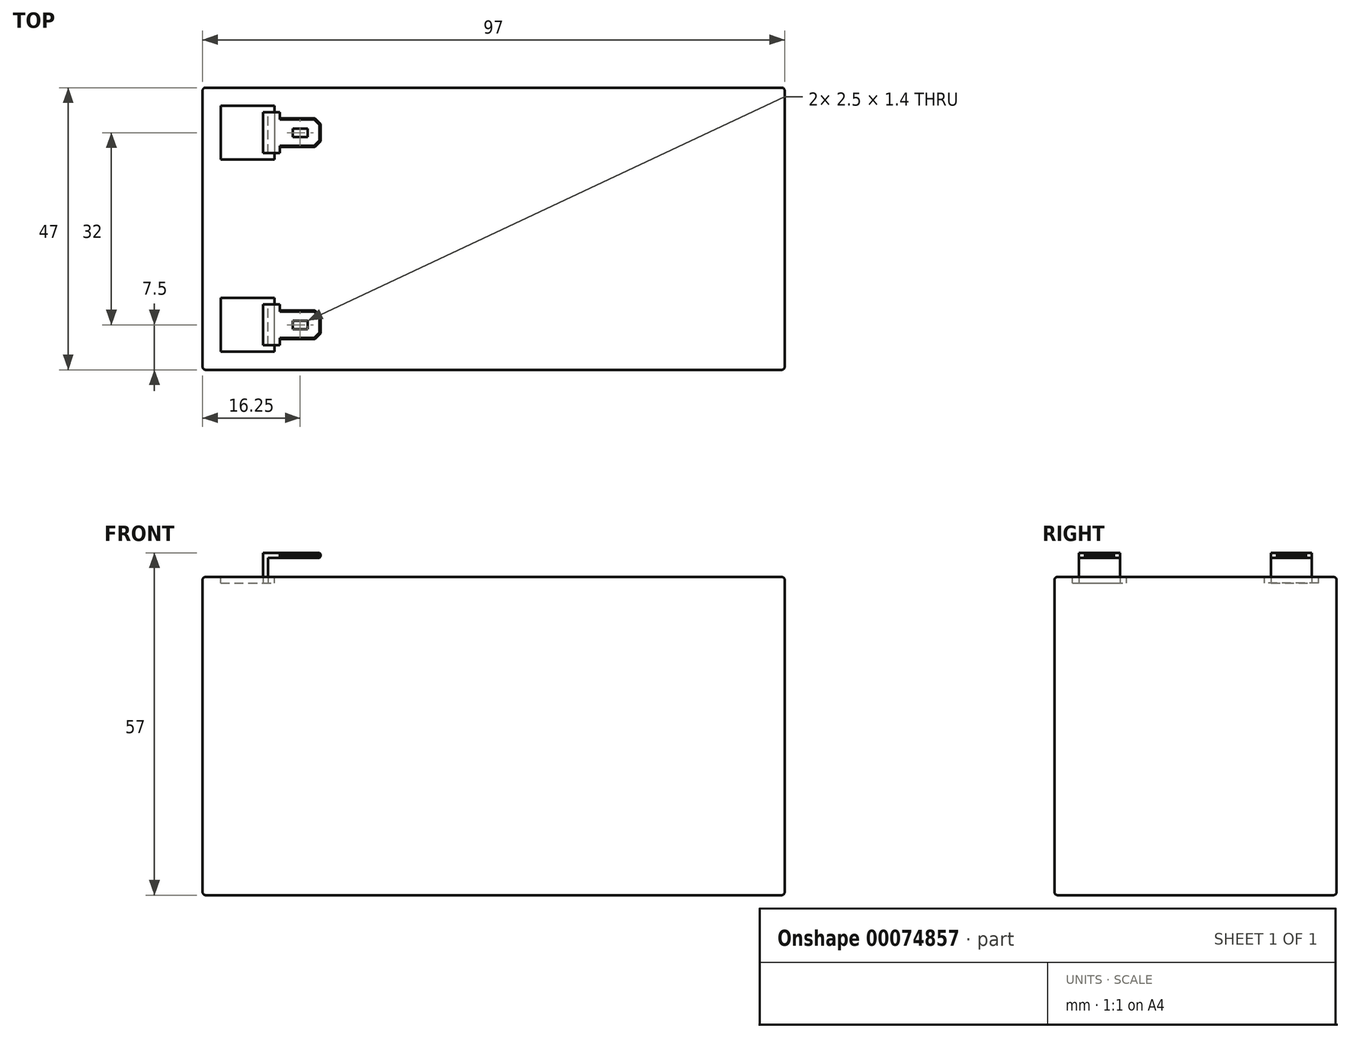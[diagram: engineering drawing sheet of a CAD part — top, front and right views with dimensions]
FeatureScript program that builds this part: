
annotation { "Feature Type Name" : "Feature", "Feature Type Description" : "" }
export const myFeature = defineFeature(function(context is Context, id is Id, definition is map)
    precondition{}
    {
        {
            var Q0;
            Q0=qCreatedBy(makeId("Top.planeOp"),FACE);
            var sketch = newSketch(context, id + "F0", { "sketchPlane" : qUnion([Q0])});
            skLineSegment(sketch, "E0.bottom", {"start": v(0, 0) * mm, "end": v(97, 0) * mm});
            skLineSegment(sketch, "E0.top", {"start": v(0, 47) * mm, "end": v(97, 47) * mm});
            skLineSegment(sketch, "E0.left", {"start": v(0, 0) * mm, "end": v(0, 47) * mm});
            skLineSegment(sketch, "E0.right", {"start": v(97, 0) * mm, "end": v(97, 47) * mm});
            skSolve(sketch);
        }
        {
            var Q0;
            Q0=makeQuery(id+"F0.imprint","IMPRINT",FACE,{"disambiguationData":[TD([[makeQuery(id+"F0.imprint","IMPRINT",EDGE,{"derivedFrom":sQuery(id+"F0.wireOp",EDGE,"E0.bottom")}),1.0]])]});
            extrude(context, id + "F1", {"entities" : qUnion([Q0]), "depth" : 53 * mm});
        }
        {
            var Q0;
            Q0=makeQuery(id+"F1.opExtrude","CAP_EDGE",EDGE,{"disambiguationData":[OSD([sQuery(id+"F0.wireOp",EDGE,"E0.right")])],"isStart":false});
            var Q1;
            Q1=makeQuery(id+"F1.opExtrude","SWEPT_EDGE",EDGE,{"disambiguationData":[OSD([sQuery(id+"F0.wireOp",EDGE,"E0.bottom"),sQuery(id+"F0.wireOp",EDGE,"E0.right")])]});
            var Q2;
            Q2=makeQuery(id+"F1.opExtrude","CAP_EDGE",EDGE,{"disambiguationData":[OSD([sQuery(id+"F0.wireOp",EDGE,"E0.right")])],"isStart":true});
            var Q3;
            Q3=makeQuery(id+"F1.opExtrude","CAP_EDGE",EDGE,{"disambiguationData":[OSD([sQuery(id+"F0.wireOp",EDGE,"E0.bottom")])],"isStart":true});
            var Q4;
            Q4=makeQuery(id+"F1.opExtrude","SWEPT_EDGE",EDGE,{"disambiguationData":[OSD([sQuery(id+"F0.wireOp",EDGE,"E0.bottom"),sQuery(id+"F0.wireOp",EDGE,"E0.left")])]});
            var Q5;
            Q5=makeQuery(id+"F1.opExtrude","CAP_EDGE",EDGE,{"disambiguationData":[OSD([sQuery(id+"F0.wireOp",EDGE,"E0.bottom")])],"isStart":false});
            var Q6;
            Q6=makeQuery(id+"F1.opExtrude","CAP_EDGE",EDGE,{"disambiguationData":[OSD([sQuery(id+"F0.wireOp",EDGE,"E0.left")])],"isStart":false});
            var Q7;
            Q7=makeQuery(id+"F1.opExtrude","CAP_EDGE",EDGE,{"disambiguationData":[OSD([sQuery(id+"F0.wireOp",EDGE,"E0.top")])],"isStart":false});
            var Q8;
            Q8=makeQuery(id+"F1.opExtrude","SWEPT_EDGE",EDGE,{"disambiguationData":[OSD([sQuery(id+"F0.wireOp",EDGE,"E0.top"),sQuery(id+"F0.wireOp",EDGE,"E0.right")])]});
            var Q9;
            Q9=makeQuery(id+"F1.opExtrude","CAP_EDGE",EDGE,{"disambiguationData":[OSD([sQuery(id+"F0.wireOp",EDGE,"E0.top")])],"isStart":true});
            var Q10;
            Q10=makeQuery(id+"F1.opExtrude","CAP_EDGE",EDGE,{"disambiguationData":[OSD([sQuery(id+"F0.wireOp",EDGE,"E0.left")])],"isStart":true});
            var Q11;
            Q11=makeQuery(id+"F1.opExtrude","SWEPT_EDGE",EDGE,{"disambiguationData":[OSD([sQuery(id+"F0.wireOp",EDGE,"E0.top"),sQuery(id+"F0.wireOp",EDGE,"E0.left")])]});
            fillet(context, id + "F2", {"entities" : qUnion([Q0, Q1, Q2, Q3, Q4, Q5, Q6, Q7, Q8, Q9, Q10, Q11]), "radius" : 0.5 * mm, "allowEdgeOverflow" : false});
        }
        {
            var Q0;
            Q0=makeQuery(id+"F1.opExtrude","CAP_FACE",FACE,{"disambiguationData":[OSD([sQuery(id+"F0.wireOp",EDGE,"E0.bottom"),sQuery(id+"F0.wireOp",EDGE,"E0.top"),sQuery(id+"F0.wireOp",EDGE,"E0.left"),sQuery(id+"F0.wireOp",EDGE,"E0.right")])],"isStart":false});
            var sketch = newSketch(context, id + "F3", { "sketchPlane" : qUnion([Q0])});
            skLineSegment(sketch, "E1.bottom", {"start": v(0, 0) * mm, "end": v(3, 0) * mm, "construction": true});
            skLineSegment(sketch, "E1.top", {"start": v(0, 3) * mm, "end": v(3, 3) * mm, "construction": true});
            skLineSegment(sketch, "E1.left", {"start": v(0, 0) * mm, "end": v(0, 3) * mm, "construction": true});
            skLineSegment(sketch, "E1.right", {"start": v(3, 0) * mm, "end": v(3, 3) * mm, "construction": true});
            skLineSegment(sketch, "E2.bottom", {"start": v(0.5, 46.5) * mm, "end": v(3, 46.5) * mm, "construction": true});
            skLineSegment(sketch, "E2.top", {"start": v(0.5, 44) * mm, "end": v(3, 44) * mm, "construction": true});
            skLineSegment(sketch, "E2.left", {"start": v(0.5, 46.5) * mm, "end": v(0.5, 44) * mm, "construction": true});
            skLineSegment(sketch, "E2.right", {"start": v(3, 46.5) * mm, "end": v(3, 44) * mm, "construction": true});
            skLineSegment(sketch, "E3.bottom", {"start": v(3, 44) * mm, "end": v(12, 44) * mm});
            skLineSegment(sketch, "E3.top", {"start": v(3, 35) * mm, "end": v(12, 35) * mm});
            skLineSegment(sketch, "E3.left", {"start": v(3, 44) * mm, "end": v(3, 35) * mm});
            skLineSegment(sketch, "E3.right", {"start": v(12, 44) * mm, "end": v(12, 35) * mm});
            skLineSegment(sketch, "E4.bottom", {"start": v(3, 3) * mm, "end": v(12, 3) * mm});
            skLineSegment(sketch, "E4.top", {"start": v(3, 12) * mm, "end": v(12, 12) * mm});
            skLineSegment(sketch, "E4.left", {"start": v(3, 3) * mm, "end": v(3, 12) * mm});
            skLineSegment(sketch, "E4.right", {"start": v(12, 3) * mm, "end": v(12, 12) * mm});
            skSolve(sketch);
        }
        {
            var Q0;
            Q0=makeQuery(id+"F3.imprint","IMPRINT",FACE,{"disambiguationData":[TD([[makeQuery(id+"F3.imprint","IMPRINT",EDGE,{"derivedFrom":sQuery(id+"F3.wireOp",EDGE,"E3.bottom")}),-1.0]])]});
            var Q1;
            Q1=makeQuery(id+"F3.imprint","IMPRINT",FACE,{"disambiguationData":[TD([[makeQuery(id+"F3.imprint","IMPRINT",EDGE,{"derivedFrom":sQuery(id+"F3.wireOp",EDGE,"E4.bottom")}),1.0]])]});
            extrude(context, id + "F4", {"entities" : qUnion([Q0, Q1]), "operationType" : NewBodyOperationType.REMOVE, "oppositeDirection" : true, "depth" : 1 * mm});
        }
        {
            var Q0;
            Q0=makeQuery(id+"F4.boolean.opBoolean","COPY",FACE,{"derivedFrom":makeQuery(id+"F4.opExtrude","CAP_FACE",FACE,{"disambiguationData":[OSD([sQuery(id+"F3.wireOp",EDGE,"E4.bottom"),sQuery(id+"F3.wireOp",EDGE,"E4.top"),sQuery(id+"F3.wireOp",EDGE,"E4.left"),sQuery(id+"F3.wireOp",EDGE,"E4.right")])],"isStart":false})});
            var sketch = newSketch(context, id + "F5", { "sketchPlane" : qUnion([Q0])});
            skLineSegment(sketch, "E5.0", {"start": v(10.9, 4.1) * mm, "end": v(10.9, 10.9) * mm});
            skLineSegment(sketch, "E6.0", {"start": v(10.1, 10.9) * mm, "end": v(10.9, 10.9) * mm});
            skLineSegment(sketch, "E7.0", {"start": v(10.1, 4.1) * mm, "end": v(10.9, 4.1) * mm});
            skLineSegment(sketch, "E8.0", {"start": v(10.1, 4.1) * mm, "end": v(10.1, 10.9) * mm});
            skLineSegment(sketch, "E9.0.1.0", {"start": v(10.1, 36.1) * mm, "end": v(10.1, 42.9) * mm});
            skLineSegment(sketch, "E9.0.1.1", {"start": v(10.1, 42.9) * mm, "end": v(10.9, 42.9) * mm});
            skLineSegment(sketch, "E9.0.1.2", {"start": v(10.9, 36.1) * mm, "end": v(10.9, 42.9) * mm});
            skLineSegment(sketch, "E9.0.1.3", {"start": v(10.1, 36.1) * mm, "end": v(10.9, 36.1) * mm});
            skLineSegment(sketch, "E9.direction1", {"start": v(10.1, 4.1) * mm, "end": v(35.1, 4.1) * mm, "construction": true});
            skLineSegment(sketch, "E9.direction2", {"start": v(10.1, 4.1) * mm, "end": v(10.1, 36.1) * mm, "construction": true});
            skSolve(sketch);
        }
        {
            var Q0;
            Q0=makeQuery(id+"F5.imprint","IMPRINT",FACE,{"disambiguationData":[TD([[makeQuery(id+"F5.imprint","IMPRINT",EDGE,{"derivedFrom":sQuery(id+"F5.wireOp",EDGE,"E9.0.1.0")}),-1.0]])]});
            var Q1;
            Q1=makeQuery(id+"F5.imprint","IMPRINT",FACE,{"disambiguationData":[TD([[makeQuery(id+"F5.imprint","IMPRINT",EDGE,{"derivedFrom":sQuery(id+"F5.wireOp",EDGE,"E5.0")}),1.0]])]});
            extrude(context, id + "F6", {"entities" : qUnion([Q0, Q1]), "operationType" : NewBodyOperationType.ADD, "depth" : 5 * mm});
        }
        {
            var Q0;
            Q0=makeQuery(id+"F6.opExtrude","SWEPT_FACE",FACE,{"disambiguationData":[OSD([sQuery(id+"F5.wireOp",EDGE,"E5.0")])]});
            var sketch = newSketch(context, id + "F7", { "sketchPlane" : qUnion([Q0])});
            skLineSegment(sketch, "E10.bottom", {"start": v(4.1, 57) * mm, "end": v(10.9, 57) * mm});
            skLineSegment(sketch, "E10.top", {"start": v(4.1, 56.2) * mm, "end": v(10.9, 56.2) * mm});
            skLineSegment(sketch, "E10.left", {"start": v(4.1, 57) * mm, "end": v(4.1, 56.2) * mm});
            skLineSegment(sketch, "E10.right", {"start": v(10.9, 57) * mm, "end": v(10.9, 56.2) * mm});
            skSolve(sketch);
        }
        {
            var Q0;
            Q0=makeQuery(id+"F6.opExtrude","SWEPT_FACE",FACE,{"disambiguationData":[OSD([sQuery(id+"F5.wireOp",EDGE,"E9.0.1.2")])]});
            var sketch = newSketch(context, id + "F8", { "sketchPlane" : qUnion([Q0])});
            skLineSegment(sketch, "E11.bottom", {"start": v(36.1, 57) * mm, "end": v(42.9, 57) * mm});
            skLineSegment(sketch, "E11.top", {"start": v(36.1, 56.2) * mm, "end": v(42.9, 56.2) * mm});
            skLineSegment(sketch, "E11.left", {"start": v(36.1, 57) * mm, "end": v(36.1, 56.2) * mm});
            skLineSegment(sketch, "E11.right", {"start": v(42.9, 57) * mm, "end": v(42.9, 56.2) * mm});
            skSolve(sketch);
        }
        {
            var Q0;
            Q0=makeQuery(id+"F8.imprint","IMPRINT",FACE,{"disambiguationData":[TD([[makeQuery(id+"F8.imprint","IMPRINT",EDGE,{"derivedFrom":sQuery(id+"F8.wireOp",EDGE,"E11.bottom")}),-1.0]])]});
            var Q1;
            Q1=makeQuery(id+"F7.imprint","IMPRINT",FACE,{"disambiguationData":[TD([[makeQuery(id+"F7.imprint","IMPRINT",EDGE,{"derivedFrom":sQuery(id+"F7.wireOp",EDGE,"E10.bottom")}),-1.0]])]});
            extrude(context, id + "F9", {"entities" : qUnion([Q0, Q1]), "operationType" : NewBodyOperationType.ADD, "depth" : 2 * mm});
        }
        {
            var Q0;
            Q0=makeQuery(id+"F9.opExtrude","CAP_FACE",FACE,{"disambiguationData":[OSD([sQuery(id+"F8.wireOp",EDGE,"E11.bottom"),sQuery(id+"F8.wireOp",EDGE,"E11.top"),sQuery(id+"F8.wireOp",EDGE,"E11.left"),sQuery(id+"F8.wireOp",EDGE,"E11.right")])],"isStart":false});
            var sketch = newSketch(context, id + "F10", { "sketchPlane" : qUnion([Q0])});
            skLineSegment(sketch, "E12.0", {"start": v(41.9, 57) * mm, "end": v(41.9, 56.2) * mm});
            skLineSegment(sketch, "E13.0", {"start": v(37.1, 57) * mm, "end": v(37.1, 56.2) * mm});
            skLineSegment(sketch, "E14.0", {"start": v(5.1, 57) * mm, "end": v(5.1, 56.2) * mm});
            skLineSegment(sketch, "E15.0", {"start": v(9.9, 57) * mm, "end": v(9.9, 56.2) * mm});
            skSolve(sketch);
        }
        {
            var Q0;
            {var subQ0=sQuery(id+"F10.wireOp",EDGE,"E12.0");Q0=makeQuery(id+"F10.imprint","IMPRINT",FACE,{"disambiguationData":[TD([[makeQuery(id+"F10.imprint","IMPRINT",EDGE,{"derivedFrom":subQ0}),-1.0]])]});}
            extrude(context, id + "F11", {"entities" : qUnion([Q0]), "operationType" : NewBodyOperationType.ADD, "depth" : 6.8 * mm});
        }
        {
            var Q0;
            Q0=makeQuery(id+"F9.opExtrude","CAP_FACE",FACE,{"disambiguationData":[OSD([sQuery(id+"F7.wireOp",EDGE,"E10.bottom"),sQuery(id+"F7.wireOp",EDGE,"E10.top"),sQuery(id+"F7.wireOp",EDGE,"E10.left"),sQuery(id+"F7.wireOp",EDGE,"E10.right")])],"isStart":false});
            var sketch = newSketch(context, id + "F12", { "sketchPlane" : qUnion([Q0])});
            skLineSegment(sketch, "E16.0", {"start": v(9.9, 57) * mm, "end": v(9.9, 56.2) * mm});
            skLineSegment(sketch, "E17.0", {"start": v(5.1, 57) * mm, "end": v(5.1, 56.2) * mm});
            skSolve(sketch);
        }
        {
            var Q0;
            {var subQ0=sQuery(id+"F12.wireOp",EDGE,"E16.0");Q0=makeQuery(id+"F12.imprint","IMPRINT",FACE,{"disambiguationData":[TD([[makeQuery(id+"F12.imprint","IMPRINT",EDGE,{"derivedFrom":subQ0}),-1.0]])]});}
            extrude(context, id + "F13", {"entities" : qUnion([Q0]), "operationType" : NewBodyOperationType.ADD, "depth" : 6.8 * mm});
        }
        {
            var Q0;
            Q0=makeQuery(id+"F13.opExtrude","CAP_EDGE",EDGE,{"disambiguationData":[OSD([sQuery(id+"F12.wireOp",EDGE,"E17.0")])],"isStart":false});
            var Q1;
            Q1=makeQuery(id+"F13.opExtrude","CAP_EDGE",EDGE,{"disambiguationData":[OSD([sQuery(id+"F12.wireOp",EDGE,"E16.0")])],"isStart":false});
            var Q2;
            Q2=makeQuery(id+"F11.opExtrude","CAP_EDGE",EDGE,{"disambiguationData":[OSD([sQuery(id+"F10.wireOp",EDGE,"E13.0")])],"isStart":false});
            var Q3;
            Q3=makeQuery(id+"F11.opExtrude","CAP_EDGE",EDGE,{"disambiguationData":[OSD([sQuery(id+"F10.wireOp",EDGE,"E12.0")])],"isStart":false});
            chamfer(context, id + "F14", {"entities" : qUnion([Q0, Q1, Q2, Q3]), "width" : 1 * mm, "tangentPropagation" : true});
        }
        {
            var Q0;
            Q0=makeQuery(id+"F13.opExtrude","SWEPT_EDGE",EDGE,{"disambiguationData":[OSD([sQuery(id+"F7.wireOp",EDGE,"E10.bottom"),sQuery(id+"F12.wireOp",EDGE,"E17.0")])]});
            var Q1;
            {var subQ0=sQuery(id+"F7.wireOp",EDGE,"E10.bottom");Q1=makeQuery(id+"F14.opChamfer","BLEND_EDGE",EDGE,{"blendedFrom":[makeQuery(id+"F13.opExtrude","CAP_EDGE",EDGE,{"disambiguationData":[OSD([sQuery(id+"F12.wireOp",EDGE,"E17.0")])],"isStart":false}),makeQuery(id+"F13.boolean.opBoolean","MERGE",FACE,{"derivedFrom":[makeQuery(id+"F9.boolean.opBoolean","MERGE",FACE,{"derivedFrom":[makeQuery(id+"F6.opExtrude","CAP_FACE",FACE,{"disambiguationData":[OSD([sQuery(id+"F5.wireOp",EDGE,"E5.0"),sQuery(id+"F5.wireOp",EDGE,"E6.0"),sQuery(id+"F5.wireOp",EDGE,"E7.0"),sQuery(id+"F5.wireOp",EDGE,"E8.0")])],"isStart":false}),makeQuery(id+"F9.opExtrude","SWEPT_FACE",FACE,{"disambiguationData":[OSD([subQ0])]})]}),makeQuery(id+"F13.opExtrude","SWEPT_FACE",FACE,{"disambiguationData":[OSD([subQ0])]})]})],"blendedInto":[makeQuery(id+"F13.boolean.opBoolean","MERGE",FACE,{"derivedFrom":[makeQuery(id+"F9.boolean.opBoolean","MERGE",FACE,{"derivedFrom":[makeQuery(id+"F6.opExtrude","CAP_FACE",FACE,{"disambiguationData":[OSD([sQuery(id+"F5.wireOp",EDGE,"E5.0"),sQuery(id+"F5.wireOp",EDGE,"E6.0"),sQuery(id+"F5.wireOp",EDGE,"E7.0"),sQuery(id+"F5.wireOp",EDGE,"E8.0")])],"isStart":false}),makeQuery(id+"F9.opExtrude","SWEPT_FACE",FACE,{"disambiguationData":[OSD([subQ0])]})]}),makeQuery(id+"F13.opExtrude","SWEPT_FACE",FACE,{"disambiguationData":[OSD([subQ0])]})]})]});}
            var Q2;
            Q2=makeQuery(id+"F13.opExtrude","CAP_EDGE",EDGE,{"disambiguationData":[OSD([sQuery(id+"F7.wireOp",EDGE,"E10.bottom")])],"isStart":false});
            var Q3;
            {var subQ0=sQuery(id+"F7.wireOp",EDGE,"E10.bottom");Q3=makeQuery(id+"F14.opChamfer","BLEND_EDGE",EDGE,{"blendedFrom":[makeQuery(id+"F13.opExtrude","CAP_EDGE",EDGE,{"disambiguationData":[OSD([sQuery(id+"F12.wireOp",EDGE,"E16.0")])],"isStart":false}),makeQuery(id+"F13.boolean.opBoolean","MERGE",FACE,{"derivedFrom":[makeQuery(id+"F9.boolean.opBoolean","MERGE",FACE,{"derivedFrom":[makeQuery(id+"F6.opExtrude","CAP_FACE",FACE,{"disambiguationData":[OSD([sQuery(id+"F5.wireOp",EDGE,"E5.0"),sQuery(id+"F5.wireOp",EDGE,"E6.0"),sQuery(id+"F5.wireOp",EDGE,"E7.0"),sQuery(id+"F5.wireOp",EDGE,"E8.0")])],"isStart":false}),makeQuery(id+"F9.opExtrude","SWEPT_FACE",FACE,{"disambiguationData":[OSD([subQ0])]})]}),makeQuery(id+"F13.opExtrude","SWEPT_FACE",FACE,{"disambiguationData":[OSD([subQ0])]})]})],"blendedInto":[makeQuery(id+"F13.boolean.opBoolean","MERGE",FACE,{"derivedFrom":[makeQuery(id+"F9.boolean.opBoolean","MERGE",FACE,{"derivedFrom":[makeQuery(id+"F6.opExtrude","CAP_FACE",FACE,{"disambiguationData":[OSD([sQuery(id+"F5.wireOp",EDGE,"E5.0"),sQuery(id+"F5.wireOp",EDGE,"E6.0"),sQuery(id+"F5.wireOp",EDGE,"E7.0"),sQuery(id+"F5.wireOp",EDGE,"E8.0")])],"isStart":false}),makeQuery(id+"F9.opExtrude","SWEPT_FACE",FACE,{"disambiguationData":[OSD([subQ0])]})]}),makeQuery(id+"F13.opExtrude","SWEPT_FACE",FACE,{"disambiguationData":[OSD([subQ0])]})]})]});}
            var Q4;
            Q4=makeQuery(id+"F13.opExtrude","SWEPT_EDGE",EDGE,{"disambiguationData":[OSD([sQuery(id+"F7.wireOp",EDGE,"E10.bottom"),sQuery(id+"F12.wireOp",EDGE,"E16.0")])]});
            var Q5;
            Q5=makeQuery(id+"F11.opExtrude","SWEPT_EDGE",EDGE,{"disambiguationData":[OSD([sQuery(id+"F8.wireOp",EDGE,"E11.bottom"),sQuery(id+"F10.wireOp",EDGE,"E13.0")])]});
            var Q6;
            {var subQ0=sQuery(id+"F8.wireOp",EDGE,"E11.bottom");Q6=makeQuery(id+"F14.opChamfer","BLEND_EDGE",EDGE,{"blendedFrom":[makeQuery(id+"F11.opExtrude","CAP_EDGE",EDGE,{"disambiguationData":[OSD([sQuery(id+"F10.wireOp",EDGE,"E13.0")])],"isStart":false}),makeQuery(id+"F11.boolean.opBoolean","MERGE",FACE,{"derivedFrom":[makeQuery(id+"F9.boolean.opBoolean","MERGE",FACE,{"derivedFrom":[makeQuery(id+"F6.opExtrude","CAP_FACE",FACE,{"disambiguationData":[OSD([sQuery(id+"F5.wireOp",EDGE,"E9.0.1.0"),sQuery(id+"F5.wireOp",EDGE,"E9.0.1.1"),sQuery(id+"F5.wireOp",EDGE,"E9.0.1.2"),sQuery(id+"F5.wireOp",EDGE,"E9.0.1.3")])],"isStart":false}),makeQuery(id+"F9.opExtrude","SWEPT_FACE",FACE,{"disambiguationData":[OSD([subQ0])]})]}),makeQuery(id+"F11.opExtrude","SWEPT_FACE",FACE,{"disambiguationData":[OSD([subQ0])]})]})],"blendedInto":[makeQuery(id+"F11.boolean.opBoolean","MERGE",FACE,{"derivedFrom":[makeQuery(id+"F9.boolean.opBoolean","MERGE",FACE,{"derivedFrom":[makeQuery(id+"F6.opExtrude","CAP_FACE",FACE,{"disambiguationData":[OSD([sQuery(id+"F5.wireOp",EDGE,"E9.0.1.0"),sQuery(id+"F5.wireOp",EDGE,"E9.0.1.1"),sQuery(id+"F5.wireOp",EDGE,"E9.0.1.2"),sQuery(id+"F5.wireOp",EDGE,"E9.0.1.3")])],"isStart":false}),makeQuery(id+"F9.opExtrude","SWEPT_FACE",FACE,{"disambiguationData":[OSD([subQ0])]})]}),makeQuery(id+"F11.opExtrude","SWEPT_FACE",FACE,{"disambiguationData":[OSD([subQ0])]})]})]});}
            var Q7;
            Q7=makeQuery(id+"F11.opExtrude","CAP_EDGE",EDGE,{"disambiguationData":[OSD([sQuery(id+"F8.wireOp",EDGE,"E11.bottom")])],"isStart":false});
            var Q8;
            {var subQ0=sQuery(id+"F8.wireOp",EDGE,"E11.bottom");Q8=makeQuery(id+"F14.opChamfer","BLEND_EDGE",EDGE,{"blendedFrom":[makeQuery(id+"F11.opExtrude","CAP_EDGE",EDGE,{"disambiguationData":[OSD([sQuery(id+"F10.wireOp",EDGE,"E12.0")])],"isStart":false}),makeQuery(id+"F11.boolean.opBoolean","MERGE",FACE,{"derivedFrom":[makeQuery(id+"F9.boolean.opBoolean","MERGE",FACE,{"derivedFrom":[makeQuery(id+"F6.opExtrude","CAP_FACE",FACE,{"disambiguationData":[OSD([sQuery(id+"F5.wireOp",EDGE,"E9.0.1.0"),sQuery(id+"F5.wireOp",EDGE,"E9.0.1.1"),sQuery(id+"F5.wireOp",EDGE,"E9.0.1.2"),sQuery(id+"F5.wireOp",EDGE,"E9.0.1.3")])],"isStart":false}),makeQuery(id+"F9.opExtrude","SWEPT_FACE",FACE,{"disambiguationData":[OSD([subQ0])]})]}),makeQuery(id+"F11.opExtrude","SWEPT_FACE",FACE,{"disambiguationData":[OSD([subQ0])]})]})],"blendedInto":[makeQuery(id+"F11.boolean.opBoolean","MERGE",FACE,{"derivedFrom":[makeQuery(id+"F9.boolean.opBoolean","MERGE",FACE,{"derivedFrom":[makeQuery(id+"F6.opExtrude","CAP_FACE",FACE,{"disambiguationData":[OSD([sQuery(id+"F5.wireOp",EDGE,"E9.0.1.0"),sQuery(id+"F5.wireOp",EDGE,"E9.0.1.1"),sQuery(id+"F5.wireOp",EDGE,"E9.0.1.2"),sQuery(id+"F5.wireOp",EDGE,"E9.0.1.3")])],"isStart":false}),makeQuery(id+"F9.opExtrude","SWEPT_FACE",FACE,{"disambiguationData":[OSD([subQ0])]})]}),makeQuery(id+"F11.opExtrude","SWEPT_FACE",FACE,{"disambiguationData":[OSD([subQ0])]})]})]});}
            var Q9;
            Q9=makeQuery(id+"F11.opExtrude","SWEPT_EDGE",EDGE,{"disambiguationData":[OSD([sQuery(id+"F8.wireOp",EDGE,"E11.bottom"),sQuery(id+"F10.wireOp",EDGE,"E12.0")])]});
            var Q10;
            Q10=makeQuery(id+"F13.opExtrude","SWEPT_EDGE",EDGE,{"disambiguationData":[OSD([sQuery(id+"F7.wireOp",EDGE,"E10.top"),sQuery(id+"F12.wireOp",EDGE,"E17.0")])]});
            var Q11;
            {var subQ0=sQuery(id+"F7.wireOp",EDGE,"E10.top");Q11=makeQuery(id+"F14.opChamfer","BLEND_EDGE",EDGE,{"blendedFrom":[makeQuery(id+"F13.opExtrude","CAP_EDGE",EDGE,{"disambiguationData":[OSD([sQuery(id+"F12.wireOp",EDGE,"E17.0")])],"isStart":false}),makeQuery(id+"F13.boolean.opBoolean","MERGE",FACE,{"derivedFrom":[makeQuery(id+"F9.opExtrude","SWEPT_FACE",FACE,{"disambiguationData":[OSD([subQ0])]}),makeQuery(id+"F13.opExtrude","SWEPT_FACE",FACE,{"disambiguationData":[OSD([subQ0])]})]})],"blendedInto":[makeQuery(id+"F13.boolean.opBoolean","MERGE",FACE,{"derivedFrom":[makeQuery(id+"F9.opExtrude","SWEPT_FACE",FACE,{"disambiguationData":[OSD([subQ0])]}),makeQuery(id+"F13.opExtrude","SWEPT_FACE",FACE,{"disambiguationData":[OSD([subQ0])]})]})]});}
            var Q12;
            Q12=makeQuery(id+"F13.opExtrude","CAP_EDGE",EDGE,{"disambiguationData":[OSD([sQuery(id+"F7.wireOp",EDGE,"E10.top")])],"isStart":false});
            var Q13;
            {var subQ0=sQuery(id+"F12.wireOp",EDGE,"E16.0");Q13=makeQuery(id+"F14.opChamfer","BLEND_EDGE",EDGE,{"blendedFrom":[makeQuery(id+"F13.opExtrude","CAP_EDGE",EDGE,{"disambiguationData":[OSD([subQ0])],"isStart":false}),makeQuery(id+"F13.opExtrude","CAP_FACE",FACE,{"disambiguationData":[OSD([sQuery(id+"F7.wireOp",EDGE,"E10.bottom"),sQuery(id+"F7.wireOp",EDGE,"E10.top"),subQ0,sQuery(id+"F12.wireOp",EDGE,"E17.0")])],"isStart":false})],"blendedInto":[makeQuery(id+"F13.opExtrude","CAP_FACE",FACE,{"disambiguationData":[OSD([sQuery(id+"F7.wireOp",EDGE,"E10.bottom"),sQuery(id+"F7.wireOp",EDGE,"E10.top"),subQ0,sQuery(id+"F12.wireOp",EDGE,"E17.0")])],"isStart":false})]});}
            var Q14;
            Q14=makeQuery(id+"F11.opExtrude","SWEPT_EDGE",EDGE,{"disambiguationData":[OSD([sQuery(id+"F8.wireOp",EDGE,"E11.top"),sQuery(id+"F10.wireOp",EDGE,"E13.0")])]});
            var Q15;
            {var subQ0=sQuery(id+"F8.wireOp",EDGE,"E11.top");Q15=makeQuery(id+"F14.opChamfer","BLEND_EDGE",EDGE,{"blendedFrom":[makeQuery(id+"F11.opExtrude","CAP_EDGE",EDGE,{"disambiguationData":[OSD([sQuery(id+"F10.wireOp",EDGE,"E13.0")])],"isStart":false}),makeQuery(id+"F11.boolean.opBoolean","MERGE",FACE,{"derivedFrom":[makeQuery(id+"F9.opExtrude","SWEPT_FACE",FACE,{"disambiguationData":[OSD([subQ0])]}),makeQuery(id+"F11.opExtrude","SWEPT_FACE",FACE,{"disambiguationData":[OSD([subQ0])]})]})],"blendedInto":[makeQuery(id+"F11.boolean.opBoolean","MERGE",FACE,{"derivedFrom":[makeQuery(id+"F9.opExtrude","SWEPT_FACE",FACE,{"disambiguationData":[OSD([subQ0])]}),makeQuery(id+"F11.opExtrude","SWEPT_FACE",FACE,{"disambiguationData":[OSD([subQ0])]})]})]});}
            var Q16;
            Q16=makeQuery(id+"F11.opExtrude","CAP_EDGE",EDGE,{"disambiguationData":[OSD([sQuery(id+"F8.wireOp",EDGE,"E11.top")])],"isStart":false});
            var Q17;
            {var subQ0=sQuery(id+"F10.wireOp",EDGE,"E12.0");Q17=makeQuery(id+"F14.opChamfer","BLEND_EDGE",EDGE,{"blendedFrom":[makeQuery(id+"F11.opExtrude","CAP_EDGE",EDGE,{"disambiguationData":[OSD([subQ0])],"isStart":false}),makeQuery(id+"F11.opExtrude","CAP_FACE",FACE,{"disambiguationData":[OSD([sQuery(id+"F8.wireOp",EDGE,"E11.bottom"),sQuery(id+"F8.wireOp",EDGE,"E11.top"),subQ0,sQuery(id+"F10.wireOp",EDGE,"E13.0")])],"isStart":false})],"blendedInto":[makeQuery(id+"F11.opExtrude","CAP_FACE",FACE,{"disambiguationData":[OSD([sQuery(id+"F8.wireOp",EDGE,"E11.bottom"),sQuery(id+"F8.wireOp",EDGE,"E11.top"),subQ0,sQuery(id+"F10.wireOp",EDGE,"E13.0")])],"isStart":false})]});}
            var Q18;
            {var subQ0=sQuery(id+"F7.wireOp",EDGE,"E10.top");Q18=makeQuery(id+"F14.opChamfer","BLEND_EDGE",EDGE,{"blendedFrom":[makeQuery(id+"F13.opExtrude","CAP_EDGE",EDGE,{"disambiguationData":[OSD([sQuery(id+"F12.wireOp",EDGE,"E16.0")])],"isStart":false}),makeQuery(id+"F13.boolean.opBoolean","MERGE",FACE,{"derivedFrom":[makeQuery(id+"F9.opExtrude","SWEPT_FACE",FACE,{"disambiguationData":[OSD([subQ0])]}),makeQuery(id+"F13.opExtrude","SWEPT_FACE",FACE,{"disambiguationData":[OSD([subQ0])]})]})],"blendedInto":[makeQuery(id+"F13.boolean.opBoolean","MERGE",FACE,{"derivedFrom":[makeQuery(id+"F9.opExtrude","SWEPT_FACE",FACE,{"disambiguationData":[OSD([subQ0])]}),makeQuery(id+"F13.opExtrude","SWEPT_FACE",FACE,{"disambiguationData":[OSD([subQ0])]})]})]});}
            var Q19;
            Q19=makeQuery(id+"F13.opExtrude","SWEPT_EDGE",EDGE,{"disambiguationData":[OSD([sQuery(id+"F7.wireOp",EDGE,"E10.top"),sQuery(id+"F12.wireOp",EDGE,"E16.0")])]});
            var Q20;
            Q20=makeQuery(id+"F11.opExtrude","SWEPT_EDGE",EDGE,{"disambiguationData":[OSD([sQuery(id+"F8.wireOp",EDGE,"E11.top"),sQuery(id+"F10.wireOp",EDGE,"E12.0")])]});
            var Q21;
            {var subQ0=sQuery(id+"F8.wireOp",EDGE,"E11.top");Q21=makeQuery(id+"F14.opChamfer","BLEND_EDGE",EDGE,{"blendedFrom":[makeQuery(id+"F11.opExtrude","CAP_EDGE",EDGE,{"disambiguationData":[OSD([sQuery(id+"F10.wireOp",EDGE,"E12.0")])],"isStart":false}),makeQuery(id+"F11.boolean.opBoolean","MERGE",FACE,{"derivedFrom":[makeQuery(id+"F9.opExtrude","SWEPT_FACE",FACE,{"disambiguationData":[OSD([subQ0])]}),makeQuery(id+"F11.opExtrude","SWEPT_FACE",FACE,{"disambiguationData":[OSD([subQ0])]})]})],"blendedInto":[makeQuery(id+"F11.boolean.opBoolean","MERGE",FACE,{"derivedFrom":[makeQuery(id+"F9.opExtrude","SWEPT_FACE",FACE,{"disambiguationData":[OSD([subQ0])]}),makeQuery(id+"F11.opExtrude","SWEPT_FACE",FACE,{"disambiguationData":[OSD([subQ0])]})]})]});}
            chamfer(context, id + "F15", {"entities" : qUnion([Q0, Q1, Q2, Q3, Q4, Q5, Q6, Q7, Q8, Q9, Q10, Q11, Q12, Q13, Q14, Q15, Q16, Q17, Q18, Q19, Q20, Q21]), "width" : 0.2 * mm, "tangentPropagation" : true});
        }
        {
            var Q0;
            {var subQ0=sQuery(id+"F8.wireOp",EDGE,"E11.bottom");Q0=makeQuery(id+"F11.boolean.opBoolean","MERGE",FACE,{"derivedFrom":[makeQuery(id+"F9.boolean.opBoolean","MERGE",FACE,{"derivedFrom":[makeQuery(id+"F6.opExtrude","CAP_FACE",FACE,{"disambiguationData":[OSD([sQuery(id+"F5.wireOp",EDGE,"E9.0.1.0"),sQuery(id+"F5.wireOp",EDGE,"E9.0.1.1"),sQuery(id+"F5.wireOp",EDGE,"E9.0.1.2"),sQuery(id+"F5.wireOp",EDGE,"E9.0.1.3")])],"isStart":false}),makeQuery(id+"F9.opExtrude","SWEPT_FACE",FACE,{"disambiguationData":[OSD([subQ0])]})]}),makeQuery(id+"F11.opExtrude","SWEPT_FACE",FACE,{"disambiguationData":[OSD([subQ0])]})]});}
            var sketch = newSketch(context, id + "F16", { "sketchPlane" : qUnion([Q0])});
            skLineSegment(sketch, "E18.0", {"start": v(17.5, 39.5) * mm, "end": v(17.5, 40.2) * mm});
            skLineSegment(sketch, "E19.0", {"start": v(17.5, 6.8) * mm, "end": v(17.5, 8.2) * mm});
            skLineSegment(sketch, "E20.0", {"start": v(15, 38.8) * mm, "end": v(15, 40.2) * mm});
            skLineSegment(sketch, "E21.0", {"start": v(15, 6.8) * mm, "end": v(15, 8.2) * mm});
            skLineSegment(sketch, "E22.0", {"start": v(15, 38.8) * mm, "end": v(17.5, 38.8) * mm});
            skLineSegment(sketch, "E23.0", {"start": v(15, 40.2) * mm, "end": v(17.5, 40.2) * mm});
            skLineSegment(sketch, "E24.0", {"start": v(15, 6.8) * mm, "end": v(17.5, 6.8) * mm});
            skLineSegment(sketch, "E25.0", {"start": v(15, 8.2) * mm, "end": v(17.5, 8.2) * mm});
            skPoint(sketch, "E26.orphan", {"position": v(17.5, 8.82) * mm});
            skPoint(sketch, "E27.orphan", {"position": v(15, 8.82) * mm});
            skPoint(sketch, "E28.orphan", {"position": v(15, 6.18) * mm});
            skPoint(sketch, "E29.orphan", {"position": v(17.5, 6.18) * mm});
            skPoint(sketch, "E30.end.orphan", {"position": v(17.5, 7.5) * mm});
            skPoint(sketch, "E30.start.orphan", {"position": v(15, 7.5) * mm});
            skPoint(sketch, "E31.end.orphan", {"position": v(17.5, 39.5) * mm});
            skPoint(sketch, "E31.start.orphan", {"position": v(15, 39.5) * mm});
            skPoint(sketch, "E32.orphan", {"position": v(17.5, 38.18) * mm});
            skPoint(sketch, "E33.orphan", {"position": v(15, 38.18) * mm});
            skPoint(sketch, "E34.orphan", {"position": v(15, 40.82) * mm});
            skPoint(sketch, "E35.orphan", {"position": v(17.5, 40.82) * mm});
            skSolve(sketch);
        }
        {
            var Q0;
            {var subQ5=sQuery(id+"F5.wireOp",EDGE,"E9.0.1.0");Q0=makeQuery(id+"F16.imprint","IMPRINT",FACE,{"disambiguationData":[TD([[makeQuery(id+"F16.imprint","IMPRINT",EDGE,{"derivedFrom":makeQuery(id+"F6.opExtrude","CAP_EDGE",EDGE,{"disambiguationData":[OSD([subQ5])],"isStart":false})}),-1.0]])]});}
            var sketch = newSketch(context, id + "F17", { "sketchPlane" : qUnion([Q0])});
            skLineSegment(sketch, "E36.bottom", {"start": v(15, 38.8) * mm, "end": v(17.5, 38.8) * mm});
            skLineSegment(sketch, "E36.top", {"start": v(15, 40.2) * mm, "end": v(17.5, 40.2) * mm});
            skLineSegment(sketch, "E36.left", {"start": v(15, 38.8) * mm, "end": v(15, 40.2) * mm});
            skLineSegment(sketch, "E36.right", {"start": v(17.5, 38.8) * mm, "end": v(17.5, 40.2) * mm});
            skSolve(sketch);
        }
        {
            var Q0;
            Q0=makeQuery(id+"F16.imprint","IMPRINT",FACE,{"disambiguationData":[TD([[makeQuery(id+"F16.imprint","IMPRINT",EDGE,{"derivedFrom":sQuery(id+"F16.wireOp",EDGE,"E19.0")}),1.0]])]});
            extrude(context, id + "F18", {"entities" : qUnion([Q0]), "operationType" : NewBodyOperationType.REMOVE, "endBound" : BoundingType.UP_TO_NEXT, "oppositeDirection" : true, "depth" : 25 * mm});
        }
        {
            var Q0;
            Q0=makeQuery(id+"F17.imprint","IMPRINT",FACE,{"disambiguationData":[TD([[makeQuery(id+"F17.imprint","IMPRINT",EDGE,{"derivedFrom":sQuery(id+"F17.wireOp",EDGE,"E36.bottom")}),1.0]])]});
            extrude(context, id + "F19", {"entities" : qUnion([Q0]), "operationType" : NewBodyOperationType.REMOVE, "endBound" : BoundingType.UP_TO_NEXT, "oppositeDirection" : true, "depth" : 25 * mm});
        }
    });
